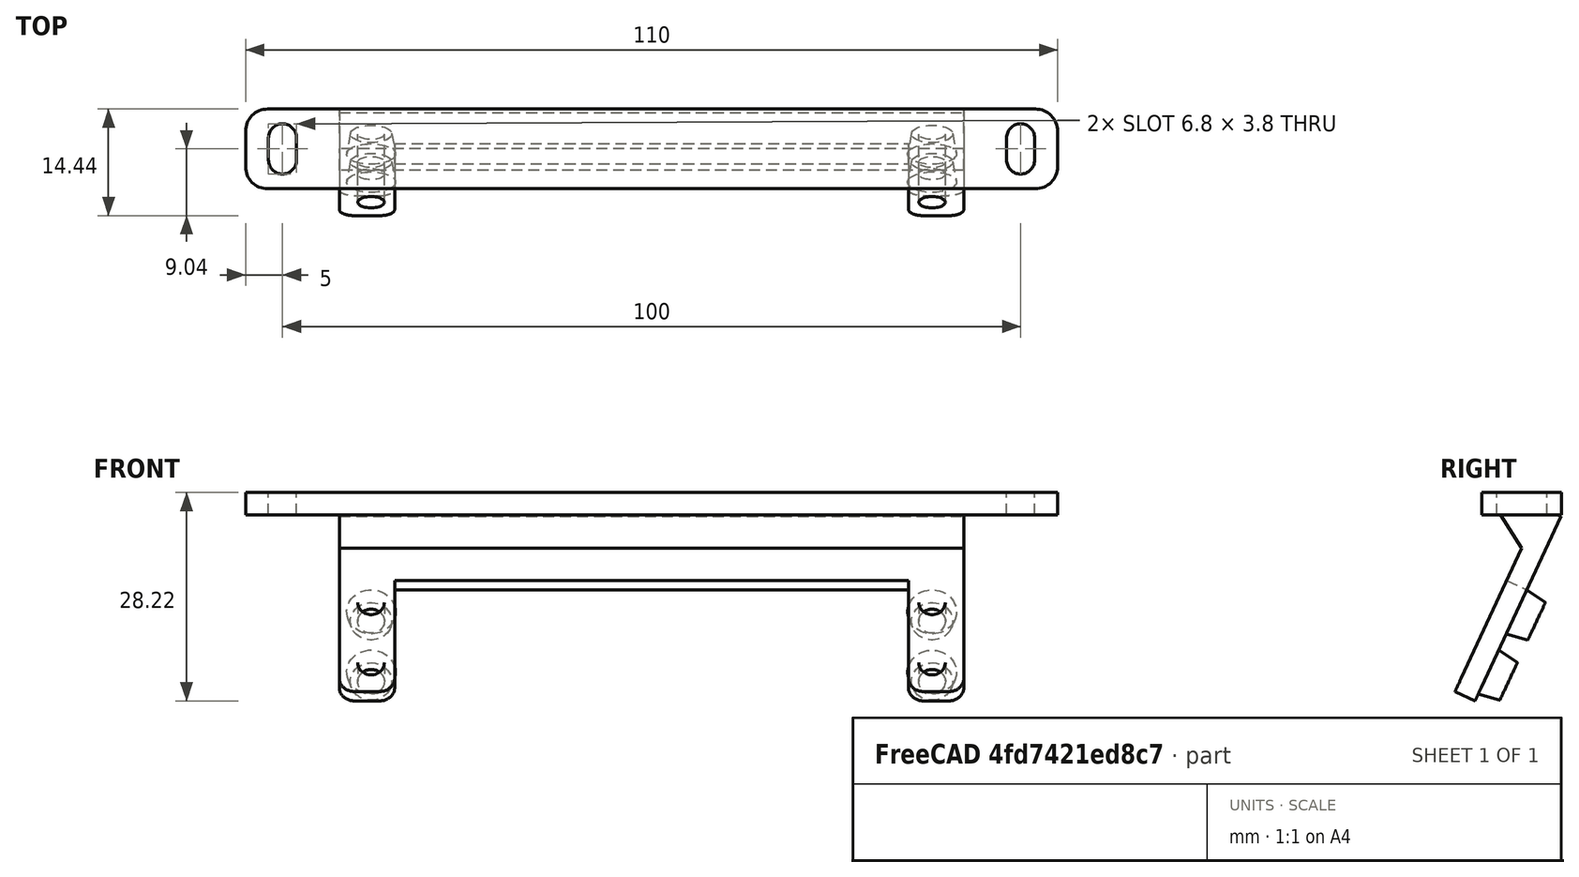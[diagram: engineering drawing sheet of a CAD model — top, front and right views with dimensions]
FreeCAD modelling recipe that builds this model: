
FCSTD DOCUMENT  (FreeCAD 0.18.4R)
Label: digits-display-3461AS1
License: FreeArt
LicenseURL: http://artlibre.org/licence/lal
objects: Part::MultiFuse×3, Part::Box×2, Part::FeaturePython×2, Spreadsheet::Sheet×1, Part::Cylinder×1, Part::Cone×1, Part::Cut×1, Part::Fillet×1, Part::Feature×1, Part::Chamfer×1
note: 13 computed .brp shape members not serialized (recipe doc carries the construction recipe); baked Part::Feature solids carry a one-line shape summary decoded from their .brp

FEATURE [Spreadsheet::Sheet] Spreadsheet  label="p"
  cells = A1=pcb_x; B1(pcb_x)=82.59999999999999; A2=pcb_y; B2(pcb_y)=15.6; A3=pcb_z; B3(pcb_z)=1.7; A4=hole_dist_x; B4(hole_dist_x)=76; A5=hole_dist_y; B5(hole_dist_y)=9; A6=side_wall; B6(side_wall)=1; A7=back_bottom_extra; B7(back_bottom_extra)=10; A8=bolt_hole_stand_wall; B8(bolt_hole_stand_wall)=1.5; A9=bolt_hole_stand_z; B9(bolt_hole_stand_z)=3; A10=bolt_hole_r; B10(bolt_hole_r)=1.8; A11=holder_width; B11(holder_width)=6.5; A12=back_wall; B12(back_wall)=3
FEATURE [Part::Box] Box006  label="lcd back holder"
  AttacherType = Attacher::AttachEngine3D
  Height = 3
  Length = 84.6
  Placement = pos=(0,-10,0) rot=(0,0,1;0rad)
  Width = 27.6
  expr: Placement.Base.y = -p.back_bottom_extra
  expr: Width = 2 * p.side_wall + p.pcb_y + p.back_bottom_extra
  expr: Height = p.back_wall
  expr: Length = 2 * p.side_wall + p.pcb_x
FEATURE [Part::Cylinder] Cylinder002  label="hole001"
  Angle = 360
  AttacherType = Attacher::AttachEngine3D
  Height = 10
  Placement = pos=(4.3,4.3,0) rot=(0,0,1;0rad)
  Radius = 1.8
  expr: Placement.Base.y = (2 * p.side_wall + p.pcb_y - p.hole_dist_y) / 2
  expr: Placement.Base.x = (2 * p.side_wall + p.pcb_x - p.hole_dist_x) / 2
  expr: Radius = p.bolt_hole_r
FEATURE [Part::FeaturePython] Array003  label="hole array001"  # Draft array (typed FeaturePython)
  Angle = 360
  ArrayType = 0
  Axis = (0,0,1)
  Base = -> Cylinder002
  Center = (0,0,0)
  Fuse = false
  IntervalAxis = (0,0,0)
  IntervalX = (76,0,0)
  IntervalY = (0,9,0)
  IntervalZ = (0,0,1)
  NumberPolar = 1
  NumberX = 2
  NumberY = 2
  NumberZ = 1
  expr: IntervalY.y = p.hole_dist_y
  expr: IntervalX.x = p.hole_dist_x
FEATURE [Part::Box] Box007  label="lcd back holder extraction"
  AttacherType = Attacher::AttachEngine3D
  Height = 3
  Length = 69.6
  Placement = pos=(7.5,1,0) rot=(0,0,1;0rad)
  Width = 31.2
  expr: Placement.Base.y = p.side_wall
  expr: Placement.Base.x = p.side_wall + p.holder_width
  expr: Width = p.pcb_y * 2 * p.side_wall
  expr: Height = p.back_wall
  expr: Length = p.pcb_x - 2 * p.holder_width
FEATURE [Part::MultiFuse] Fusion002  label="back extraction fusion"
  Shapes = -> [Array003,Box007]
FEATURE [Part::Cone] Cone  label="hole stand cone"
  Angle = 360
  AttacherType = Attacher::AttachEngine3D
  Height = 3
  Placement = pos=(4.3,4.3,3) rot=(0,0,1;0rad)
  Radius1 = 3.3
  Radius2 = 2.8
  expr: Height = p.bolt_hole_stand_z
  expr: Placement.Base.z = p.back_wall
  expr: Placement.Base.y = (2 * p.side_wall + p.pcb_y - p.hole_dist_y) / 2
  expr: Placement.Base.x = (2 * p.side_wall + p.pcb_x - p.hole_dist_x) / 2
  expr: Radius2 = p.bolt_hole_r + p.bolt_hole_stand_wall - 0.5
  expr: Radius1 = p.bolt_hole_r + p.bolt_hole_stand_wall
FEATURE [Part::FeaturePython] Array004  label="hole array002"  # Draft array (typed FeaturePython)
  Angle = 360
  ArrayType = 0
  Axis = (0,0,1)
  Base = -> Cone
  Center = (0,0,0)
  Fuse = false
  IntervalAxis = (0,0,0)
  IntervalX = (76,0,0)
  IntervalY = (0,9,0)
  IntervalZ = (0,0,1)
  NumberPolar = 1
  NumberX = 2
  NumberY = 2
  NumberZ = 1
  expr: IntervalY.y = p.hole_dist_y
  expr: IntervalX.x = p.hole_dist_x
FEATURE [Part::MultiFuse] Fusion  label="lcd back holder fusion"
  Shapes = -> [Box006,Array004]
FEATURE [Part::Cut] Cut003  label="back cut"
  Base = -> Fusion
  Tool = -> Fusion002
FEATURE [Part::Fillet] Fillet003  label="back cut fillet"
  Base = -> Cut003
  Edges = 4 edges r=2: [Edge3,Edge25,Edge35,Edge50]
  Placement = pos=(0,6.2,-8) rot=(-1,0,0;2.00713rad)
FEATURE [Part::Feature] Cut003002  label="attach plane x dir002"
  shape: bbox 110 x 10.8 x 3 mm, 18 faces (baked)
FEATURE [Part::MultiFuse] Fusion003  label="display fusion"
  Shapes = -> [Cut003002,Fillet003]
FEATURE [Part::Chamfer] Chamfer  label="display chamber"
  Base = -> Fusion003
  Edges = 1 edges r=5: [Edge29]
